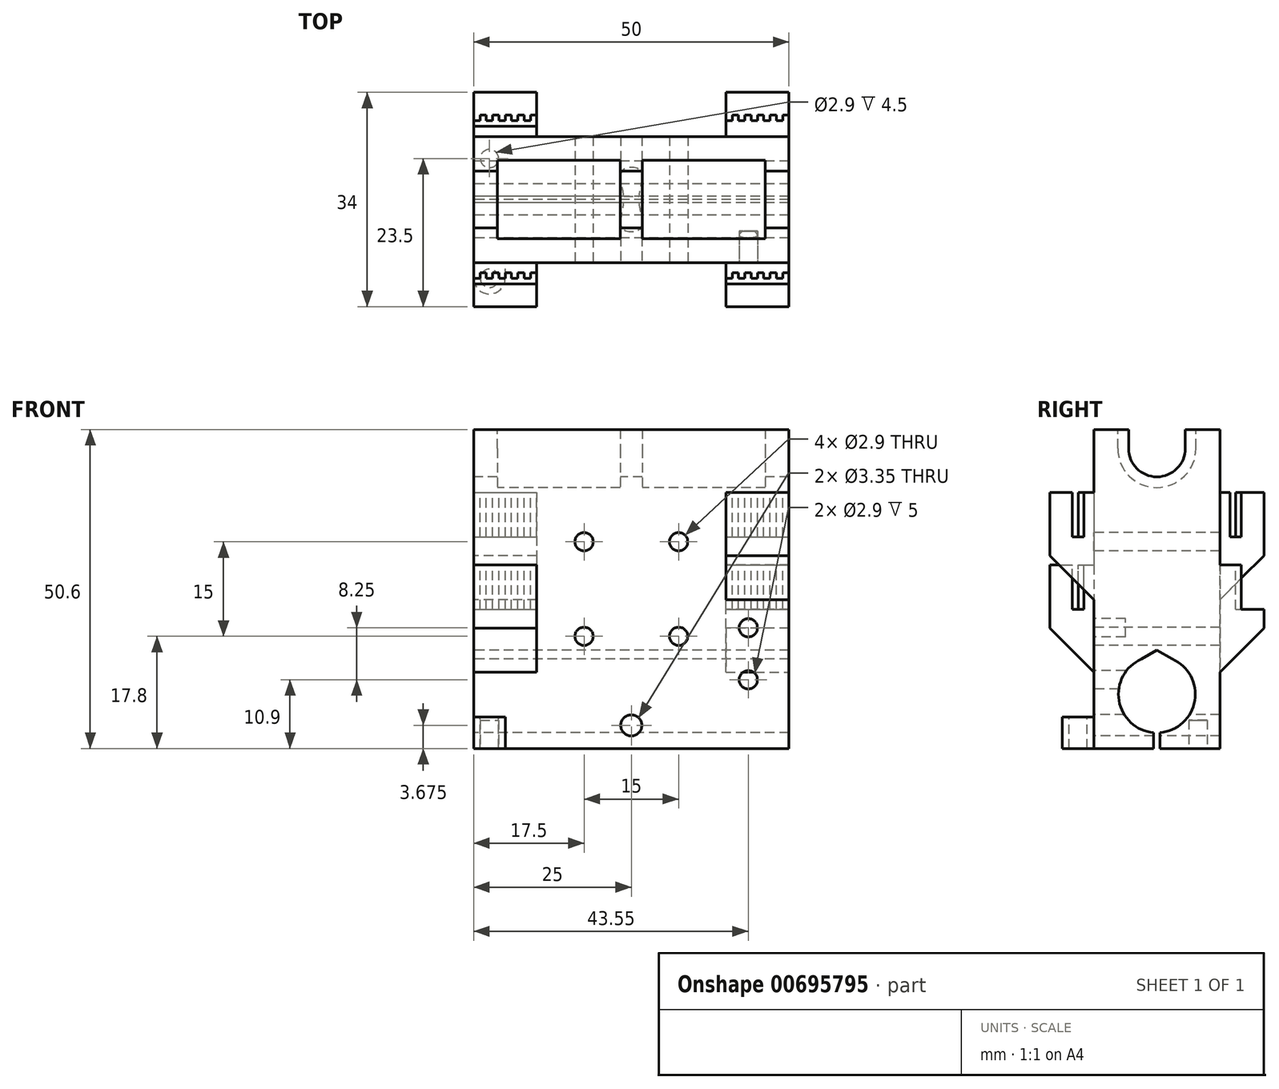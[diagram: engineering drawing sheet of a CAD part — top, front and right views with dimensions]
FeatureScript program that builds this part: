
annotation { "Feature Type Name" : "Feature", "Feature Type Description" : "" }
export const myFeature = defineFeature(function(context is Context, id is Id, definition is map)
    precondition{}
    {
        {
            var Q0;
            Q0=qCreatedBy(makeId("Top.planeOp"),FACE);
            var sketch = newSketch(context, id + "F0", { "sketchPlane" : qUnion([Q0])});
            skLineSegment(sketch, "E0.bottom", {"start": v(0, 0) * mm, "end": v(50, 0) * mm});
            skLineSegment(sketch, "E0.top", {"start": v(0, 20) * mm, "end": v(50, 20) * mm});
            skLineSegment(sketch, "E0.left", {"start": v(0, 0) * mm, "end": v(0, 20) * mm});
            skLineSegment(sketch, "E0.right", {"start": v(50, 0) * mm, "end": v(50, 20) * mm});
            skSolve(sketch);
        }
        {
            var Q0;
            Q0=qSketchRegion(id+"F0",true);
            extrude(context, id + "F1", {"entities" : qUnion([Q0]), "depth" : 50.6 * mm});
        }
        {
            var Q0;
            Q0=makeQuery(id+"F1.opExtrude","SWEPT_FACE",FACE,{"disambiguationData":[OSD([sQuery(id+"F0.wireOp",EDGE,"E0.left")])]});
            var sketch = newSketch(context, id + "F2", { "sketchPlane" : qUnion([Q0])});
            skCircle(sketch, "E1", {"center": v(-10, 8.6) * mm, "radius": 6.1 * mm});
            skCircle(sketch, "E2", {"center": v(-10, 47.6) * mm, "radius": 4.5 * mm});
            skLineSegment(sketch, "E3", {"start": v(-20, 47.6) * mm, "end": v(0, 47.6) * mm, "construction": true});
            skLineSegment(sketch, "E4", {"start": v(-14.5, 50.6) * mm, "end": v(-14.5, 47.6) * mm});
            skLineSegment(sketch, "E5", {"start": v(-5.5, 50.6) * mm, "end": v(-5.5, 47.6) * mm});
            skLineSegment(sketch, "E6", {"start": v(-20, 8.6) * mm, "end": v(0, 8.6) * mm, "construction": true});
            skLineSegment(sketch, "E7", {"start": v(-10, 8.6) * mm, "end": v(-10, 0) * mm, "construction": true});
            skLineSegment(sketch, "E8", {"start": v(-10, 0) * mm, "end": v(-10.5, 0) * mm});
            skLineSegment(sketch, "E9", {"start": v(-10.5, 0) * mm, "end": v(-10.5, 2.52) * mm});
            skLineSegment(sketch, "E10", {"start": v(-10.5, 2.52) * mm, "end": v(-9.5, 2.52) * mm});
            skLineSegment(sketch, "E11", {"start": v(-9.5, 2.52) * mm, "end": v(-9.5, 0) * mm});
            skLineSegment(sketch, "E12", {"start": v(-9.5, 0) * mm, "end": v(-10, 0) * mm});
            skLineSegment(sketch, "E13", {"start": v(-10, 14.7) * mm, "end": v(-10, 15.6) * mm});
            skLineSegment(sketch, "E14", {"start": v(-10, 15.6) * mm, "end": v(-6.39, 13.51) * mm});
            skLineSegment(sketch, "E15", {"start": v(-10, 15.6) * mm, "end": v(-13.61, 13.51) * mm});
            skCircle(sketch, "E16", {"center": v(-10, 47.6) * mm, "radius": 6.2 * mm});
            skLineSegment(sketch, "E17", {"start": v(-3.8, 47.6) * mm, "end": v(-3.8, 50.6) * mm});
            skLineSegment(sketch, "E18", {"start": v(-16.2, 47.6) * mm, "end": v(-16.2, 50.6) * mm});
            skSolve(sketch);
        }
        {
            var Q0;
            {var subQ0=sQuery(id+"F2.wireOp",EDGE,"E14");var subQ1=sQuery(id+"F2.wireOp",EDGE,"E1");var subQ3=makeQuery(id+"F2.imprint","INTERSECT",VERTEX,{"disambiguationData":[OD(0.0)],"derivedFrom":[subQ1,subQ0]});Q0=makeQuery(id+"F2.imprint","IMPRINT",FACE,{"disambiguationData":[TD([[makeQuery(id+"F2.imprint","IMPRINT",EDGE,{"disambiguationData":[TD([[subQ3,-1.0]])],"derivedFrom":subQ1}),1.0]])]});}
            var Q1;
            {var subQ0=sQuery(id+"F2.wireOp",EDGE,"E15");var subQ1=sQuery(id+"F2.wireOp",EDGE,"E1");var subQ3=makeQuery(id+"F2.imprint","INTERSECT",VERTEX,{"disambiguationData":[OD(0.0)],"derivedFrom":[subQ1,subQ0]});Q1=makeQuery(id+"F2.imprint","IMPRINT",FACE,{"disambiguationData":[TD([[makeQuery(id+"F2.imprint","IMPRINT",EDGE,{"disambiguationData":[TD([[subQ3,1.0]])],"derivedFrom":subQ1}),1.0]])]});}
            var Q2;
            Q2=makeQuery(id+"F2.imprint","IMPRINT",FACE,{"disambiguationData":[TD([[makeQuery(id+"F2.imprint","IMPRINT",EDGE,{"derivedFrom":sQuery(id+"F2.wireOp",EDGE,"E8")}),-1.0]])]});
            var Q3;
            {var subQ0=sQuery(id+"F2.wireOp",EDGE,"E10");Q3=makeQuery(id+"F2.imprint","IMPRINT",FACE,{"disambiguationData":[TD([[makeQuery(id+"F2.imprint","IMPRINT",EDGE,{"derivedFrom":subQ0}),-1.0]])]});}
            var Q4;
            {var subQ3=sQuery(id+"F2.wireOp",EDGE,"E13");Q4=makeQuery(id+"F2.imprint","IMPRINT",FACE,{"disambiguationData":[TD([[makeQuery(id+"F2.imprint","IMPRINT",EDGE,{"derivedFrom":subQ3}),-1.0]])]});}
            var Q5;
            {var subQ3=sQuery(id+"F2.wireOp",EDGE,"E13");Q5=makeQuery(id+"F2.imprint","IMPRINT",FACE,{"disambiguationData":[TD([[makeQuery(id+"F2.imprint","IMPRINT",EDGE,{"derivedFrom":subQ3}),1.0]])]});}
            var Q6;
            {var subQ7=sQuery(id+"F2.wireOp",EDGE,"E10");Q6=makeQuery(id+"F2.imprint","IMPRINT",FACE,{"disambiguationData":[TD([[makeQuery(id+"F2.imprint","IMPRINT",EDGE,{"derivedFrom":subQ7}),1.0]])]});}
            var Q7;
            {var subQ3=sQuery(id+"F2.wireOp",EDGE,"E5");Q7=makeQuery(id+"F2.imprint","IMPRINT",FACE,{"disambiguationData":[TD([[makeQuery(id+"F2.imprint","IMPRINT",EDGE,{"derivedFrom":subQ3}),-1.0]])]});}
            var Q8;
            {var subQ0=sQuery(id+"F2.wireOp",EDGE,"E4");Q8=makeQuery(id+"F2.imprint","IMPRINT",FACE,{"disambiguationData":[TD([[makeQuery(id+"F2.imprint","IMPRINT",EDGE,{"derivedFrom":subQ0}),1.0]])]});}
            var Q9;
            {var subQ0=sQuery(id+"F2.wireOp",EDGE,"E4");Q9=makeQuery(id+"F2.imprint","IMPRINT",FACE,{"disambiguationData":[TD([[makeQuery(id+"F2.imprint","IMPRINT",EDGE,{"derivedFrom":subQ0}),1.0]])]});}
            var Q10;
            {var subQ3=sQuery(id+"F2.wireOp",EDGE,"E5");Q10=makeQuery(id+"F2.imprint","IMPRINT",FACE,{"disambiguationData":[TD([[makeQuery(id+"F2.imprint","IMPRINT",EDGE,{"derivedFrom":subQ3}),-1.0]])]});}
            var Q11;
            {var subQ1=sQuery(id+"F2.wireOp",EDGE,"E2");var subQ4=makeQuery(id+"F2.imprint","INTERSECT",VERTEX,{"derivedFrom":[subQ1,sQuery(id+"F2.wireOp",EDGE,"E5")]});Q11=makeQuery(id+"F2.imprint","IMPRINT",FACE,{"disambiguationData":[TD([[makeQuery(id+"F2.imprint","IMPRINT",EDGE,{"disambiguationData":[TD([[subQ4,-1.0]])],"derivedFrom":subQ1}),1.0]])]});}
            extrude(context, id + "F3", {"entities" : qUnion([Q0, Q1, Q2, Q3, Q4, Q5, Q6, Q7, Q8, Q9, Q10, Q11]), "operationType" : NewBodyOperationType.REMOVE, "endBound" : BoundingType.THROUGH_ALL, "oppositeDirection" : true, "depth" : 25 * mm});
        }
        {
            var Q0;
            {var subQ3=sQuery(id+"F2.wireOp",EDGE,"E4");Q0=makeQuery(id+"F2.imprint","IMPRINT",FACE,{"disambiguationData":[TD([[makeQuery(id+"F2.imprint","IMPRINT",EDGE,{"derivedFrom":subQ3}),-1.0]])]});}
            var Q1;
            {var subQ3=sQuery(id+"F2.wireOp",EDGE,"E18");Q1=makeQuery(id+"F2.imprint","IMPRINT",FACE,{"disambiguationData":[TD([[makeQuery(id+"F2.imprint","IMPRINT",EDGE,{"derivedFrom":subQ3}),-1.0]])]});}
            var Q2;
            {var subQ3=sQuery(id+"F2.wireOp",EDGE,"E17");Q2=makeQuery(id+"F2.imprint","IMPRINT",FACE,{"disambiguationData":[TD([[makeQuery(id+"F2.imprint","IMPRINT",EDGE,{"derivedFrom":subQ3}),1.0]])]});}
            extrude(context, id + "F4", {"entities" : qUnion([Q0, Q1, Q2]), "operationType" : NewBodyOperationType.REMOVE, "oppositeDirection" : true, "depth" : 46.25 * mm});
        }
        {
            var Q0;
            {var subQ3=sQuery(id+"F2.wireOp",EDGE,"E4");Q0=makeQuery(id+"F2.imprint","IMPRINT",FACE,{"disambiguationData":[TD([[makeQuery(id+"F2.imprint","IMPRINT",EDGE,{"derivedFrom":subQ3}),-1.0]])]});}
            var Q1;
            {var subQ3=sQuery(id+"F2.wireOp",EDGE,"E18");Q1=makeQuery(id+"F2.imprint","IMPRINT",FACE,{"disambiguationData":[TD([[makeQuery(id+"F2.imprint","IMPRINT",EDGE,{"derivedFrom":subQ3}),-1.0]])]});}
            var Q2;
            {var subQ3=sQuery(id+"F2.wireOp",EDGE,"E17");Q2=makeQuery(id+"F2.imprint","IMPRINT",FACE,{"disambiguationData":[TD([[makeQuery(id+"F2.imprint","IMPRINT",EDGE,{"derivedFrom":subQ3}),1.0]])]});}
            extrude(context, id + "F5", {"entities" : qUnion([Q0, Q1, Q2]), "operationType" : NewBodyOperationType.ADD, "oppositeDirection" : true, "depth" : 26.75 * mm});
        }
        {
            var Q0;
            {var subQ3=sQuery(id+"F2.wireOp",EDGE,"E4");Q0=makeQuery(id+"F2.imprint","IMPRINT",FACE,{"disambiguationData":[TD([[makeQuery(id+"F2.imprint","IMPRINT",EDGE,{"derivedFrom":subQ3}),-1.0]])]});}
            var Q1;
            {var subQ3=sQuery(id+"F2.wireOp",EDGE,"E18");Q1=makeQuery(id+"F2.imprint","IMPRINT",FACE,{"disambiguationData":[TD([[makeQuery(id+"F2.imprint","IMPRINT",EDGE,{"derivedFrom":subQ3}),-1.0]])]});}
            var Q2;
            {var subQ3=sQuery(id+"F2.wireOp",EDGE,"E17");Q2=makeQuery(id+"F2.imprint","IMPRINT",FACE,{"disambiguationData":[TD([[makeQuery(id+"F2.imprint","IMPRINT",EDGE,{"derivedFrom":subQ3}),1.0]])]});}
            extrude(context, id + "F6", {"entities" : qUnion([Q0, Q1, Q2]), "operationType" : NewBodyOperationType.REMOVE, "oppositeDirection" : true, "depth" : 23.25 * mm});
        }
        {
            var Q0;
            {var subQ3=sQuery(id+"F2.wireOp",EDGE,"E4");Q0=makeQuery(id+"F2.imprint","IMPRINT",FACE,{"disambiguationData":[TD([[makeQuery(id+"F2.imprint","IMPRINT",EDGE,{"derivedFrom":subQ3}),-1.0]])]});}
            var Q1;
            {var subQ3=sQuery(id+"F2.wireOp",EDGE,"E18");Q1=makeQuery(id+"F2.imprint","IMPRINT",FACE,{"disambiguationData":[TD([[makeQuery(id+"F2.imprint","IMPRINT",EDGE,{"derivedFrom":subQ3}),-1.0]])]});}
            var Q2;
            {var subQ3=sQuery(id+"F2.wireOp",EDGE,"E17");Q2=makeQuery(id+"F2.imprint","IMPRINT",FACE,{"disambiguationData":[TD([[makeQuery(id+"F2.imprint","IMPRINT",EDGE,{"derivedFrom":subQ3}),1.0]])]});}
            extrude(context, id + "F7", {"entities" : qUnion([Q0, Q1, Q2]), "operationType" : NewBodyOperationType.ADD, "oppositeDirection" : true, "depth" : 3.75 * mm});
        }
        {
            var Q0;
            Q0=makeQuery(id+"F1.opExtrude","SWEPT_FACE",FACE,{"disambiguationData":[OSD([sQuery(id+"F0.wireOp",EDGE,"E0.bottom")])]});
            var sketch = newSketch(context, id + "F8", { "sketchPlane" : qUnion([Q0])});
            skLineSegment(sketch, "E19.bottom", {"start": v(0, 29.1) * mm, "end": v(10, 29.1) * mm});
            skLineSegment(sketch, "E19.top", {"start": v(0, 9.1) * mm, "end": v(10, 9.1) * mm});
            skLineSegment(sketch, "E19.left", {"start": v(0, 29.1) * mm, "end": v(0, 9.1) * mm});
            skLineSegment(sketch, "E19.right", {"start": v(10, 29.1) * mm, "end": v(10, 9.1) * mm});
            skLineSegment(sketch, "E20.bottom", {"start": v(50, 40.6) * mm, "end": v(40, 40.6) * mm});
            skLineSegment(sketch, "E20.top", {"start": v(50, 20.6) * mm, "end": v(40, 20.6) * mm});
            skLineSegment(sketch, "E20.left", {"start": v(50, 40.6) * mm, "end": v(50, 20.6) * mm});
            skLineSegment(sketch, "E20.right", {"start": v(40, 40.6) * mm, "end": v(40, 20.6) * mm});
            skPoint(sketch, "E21", {"position": v(0, 47.6) * mm});
            skPoint(sketch, "E22", {"position": v(0, 8.6) * mm});
            skSolve(sketch);
        }
        {
            var Q0;
            Q0=qSketchRegion(id+"F8",true);
            extrude(context, id + "F9", {"entities" : qUnion([Q0]), "operationType" : NewBodyOperationType.ADD, "depth" : 7 * mm});
        }
        {
            var Q0;
            Q0=makeQuery(id+"F9.opExtrude","CAP_EDGE",EDGE,{"disambiguationData":[OSD([sQuery(id+"F8.wireOp",EDGE,"E19.top")])],"isStart":false});
            var Q1;
            Q1=makeQuery(id+"F9.opExtrude","CAP_EDGE",EDGE,{"disambiguationData":[OSD([sQuery(id+"F8.wireOp",EDGE,"E20.top")])],"isStart":false});
            chamfer(context, id + "F10", {"entities" : qUnion([Q0, Q1]), "width" : 10 * mm, "tangentPropagation" : true});
        }
        {
            var Q0;
            Q0=makeQuery(id+"F9.opExtrude","SWEPT_FACE",FACE,{"disambiguationData":[OSD([sQuery(id+"F8.wireOp",EDGE,"E19.bottom")])]});
            var sketch = newSketch(context, id + "F11", { "sketchPlane" : qUnion([Q0])});
            skLineSegment(sketch, "E23", {"start": v(-935.9, 0) * mm, "end": v(-935.88, -4.54) * mm});
            skLineSegment(sketch, "E24.left", {"start": v(0, -3.4) * mm, "end": v(0, -1.6) * mm});
            skLineSegment(sketch, "E25", {"start": v(6, -2.5) * mm, "end": v(7, -2.5) * mm});
            skLineSegment(sketch, "E26", {"start": v(4, -2.5) * mm, "end": v(5, -2.5) * mm});
            skLineSegment(sketch, "E27", {"start": v(0, -2.5) * mm, "end": v(1, -2.5) * mm});
            skLineSegment(sketch, "E28", {"start": v(7, -1.6) * mm, "end": v(8, -1.6) * mm});
            skLineSegment(sketch, "E29", {"start": v(2, -2.5) * mm, "end": v(3, -2.5) * mm});
            skLineSegment(sketch, "E30", {"start": v(3, -1.6) * mm, "end": v(4, -1.6) * mm});
            skLineSegment(sketch, "E31", {"start": v(8, -2.5) * mm, "end": v(9, -2.5) * mm});
            skLineSegment(sketch, "E32", {"start": v(8, -1.6) * mm, "end": v(8, -2.5) * mm});
            skLineSegment(sketch, "E33", {"start": v(9, -2.5) * mm, "end": v(9, -1.6) * mm});
            skLineSegment(sketch, "E34", {"start": v(10, -1.6) * mm, "end": v(10, -2.5) * mm});
            skLineSegment(sketch, "E35", {"start": v(6, -1.6) * mm, "end": v(6, -2.5) * mm});
            skLineSegment(sketch, "E36", {"start": v(2, -1.6) * mm, "end": v(2, -2.5) * mm});
            skLineSegment(sketch, "E37", {"start": v(1, -1.6) * mm, "end": v(2, -1.6) * mm});
            skLineSegment(sketch, "E38", {"start": v(1, -2.5) * mm, "end": v(1, -1.6) * mm});
            skLineSegment(sketch, "E39", {"start": v(9, -1.6) * mm, "end": v(10, -1.6) * mm});
            skLineSegment(sketch, "E40", {"start": v(5, -1.6) * mm, "end": v(6, -1.6) * mm});
            skLineSegment(sketch, "E41", {"start": v(5, -2.5) * mm, "end": v(5, -1.6) * mm});
            skLineSegment(sketch, "E42", {"start": v(3, -2.5) * mm, "end": v(3, -1.6) * mm});
            skLineSegment(sketch, "E43", {"start": v(4, -1.6) * mm, "end": v(4, -2.5) * mm});
            skLineSegment(sketch, "E44", {"start": v(7, -2.5) * mm, "end": v(7, -1.6) * mm});
            skLineSegment(sketch, "E45", {"start": v(0, -1.6) * mm, "end": v(0, -2.5) * mm});
            skLineSegment(sketch, "E46", {"start": v(10, -2.5) * mm, "end": v(10, -3.4) * mm});
            skLineSegment(sketch, "E47", {"start": v(0, -3.4) * mm, "end": v(10, -3.4) * mm});
            skLineSegment(sketch, "E48", {"start": v(5.3, -1.6) * mm, "end": v(5.3, 0) * mm});
            skSolve(sketch);
        }
        {
            var Q0;
            Q0=qSketchRegion(id+"F11",true);
            extrude(context, id + "F12", {"entities" : qUnion([Q0]), "operationType" : NewBodyOperationType.REMOVE, "oppositeDirection" : true, "depth" : 7 * mm});
        }
        {
            var Q0;
            Q0=makeQuery(id+"F9.opExtrude","SWEPT_FACE",FACE,{"disambiguationData":[OSD([sQuery(id+"F8.wireOp",EDGE,"E20.bottom")])]});
            var sketch = newSketch(context, id + "F13", { "sketchPlane" : qUnion([Q0])});
            skLineSegment(sketch, "E49.left", {"start": v(40, -3.4) * mm, "end": v(40, -1.6) * mm});
            skLineSegment(sketch, "E50", {"start": v(46, -2.5) * mm, "end": v(47, -2.5) * mm});
            skLineSegment(sketch, "E51", {"start": v(44, -2.5) * mm, "end": v(45, -2.5) * mm});
            skLineSegment(sketch, "E52", {"start": v(40, -2.5) * mm, "end": v(41, -2.5) * mm});
            skLineSegment(sketch, "E53", {"start": v(47, -1.6) * mm, "end": v(48, -1.6) * mm});
            skLineSegment(sketch, "E54", {"start": v(42, -2.5) * mm, "end": v(43, -2.5) * mm});
            skLineSegment(sketch, "E55", {"start": v(43, -1.6) * mm, "end": v(44, -1.6) * mm});
            skLineSegment(sketch, "E56", {"start": v(48, -2.5) * mm, "end": v(49, -2.5) * mm});
            skLineSegment(sketch, "E57", {"start": v(48, -1.6) * mm, "end": v(48, -2.5) * mm});
            skLineSegment(sketch, "E58", {"start": v(49, -2.5) * mm, "end": v(49, -1.6) * mm});
            skLineSegment(sketch, "E59", {"start": v(50, -1.6) * mm, "end": v(50, -2.5) * mm});
            skLineSegment(sketch, "E60", {"start": v(46, -1.6) * mm, "end": v(46, -2.5) * mm});
            skLineSegment(sketch, "E61", {"start": v(42, -1.6) * mm, "end": v(42, -2.5) * mm});
            skLineSegment(sketch, "E62", {"start": v(41, -1.6) * mm, "end": v(42, -1.6) * mm});
            skLineSegment(sketch, "E63", {"start": v(41, -2.5) * mm, "end": v(41, -1.6) * mm});
            skLineSegment(sketch, "E64", {"start": v(49, -1.6) * mm, "end": v(50, -1.6) * mm});
            skLineSegment(sketch, "E65", {"start": v(45, -1.6) * mm, "end": v(46, -1.6) * mm});
            skLineSegment(sketch, "E66", {"start": v(45, -2.5) * mm, "end": v(45, -1.6) * mm});
            skLineSegment(sketch, "E67", {"start": v(43, -2.5) * mm, "end": v(43, -1.6) * mm});
            skLineSegment(sketch, "E68", {"start": v(44, -1.6) * mm, "end": v(44, -2.5) * mm});
            skLineSegment(sketch, "E69", {"start": v(47, -2.5) * mm, "end": v(47, -1.6) * mm});
            skLineSegment(sketch, "E70", {"start": v(40, -1.6) * mm, "end": v(40, -2.5) * mm});
            skLineSegment(sketch, "E71", {"start": v(50, -2.5) * mm, "end": v(50, -3.4) * mm});
            skLineSegment(sketch, "E72", {"start": v(40, -3.4) * mm, "end": v(50, -3.4) * mm});
            skLineSegment(sketch, "E73", {"start": v(45.23, -1.6) * mm, "end": v(45.23, 0) * mm});
            skSolve(sketch);
        }
        {
            var Q0;
            Q0=qSketchRegion(id+"F13",true);
            extrude(context, id + "F14", {"entities" : qUnion([Q0]), "operationType" : NewBodyOperationType.REMOVE, "oppositeDirection" : true, "depth" : 7 * mm});
        }
        {
            var Q0;
            Q0=makeQuery(id+"F1.opExtrude","SWEPT_FACE",FACE,{"disambiguationData":[OSD([sQuery(id+"F0.wireOp",EDGE,"E0.top")])]});
            var sketch = newSketch(context, id + "F15", { "sketchPlane" : qUnion([Q0])});
            skLineSegment(sketch, "E74.bottom", {"start": v(-50, 9.1) * mm, "end": v(-40, 9.1) * mm});
            skLineSegment(sketch, "E74.top", {"start": v(-50, 29.1) * mm, "end": v(-40, 29.1) * mm});
            skLineSegment(sketch, "E74.left", {"start": v(-50, 9.1) * mm, "end": v(-50, 29.1) * mm});
            skLineSegment(sketch, "E74.right", {"start": v(-40, 9.1) * mm, "end": v(-40, 29.1) * mm});
            skLineSegment(sketch, "E75.bottom", {"start": v(0, 40.6) * mm, "end": v(-10, 40.6) * mm});
            skLineSegment(sketch, "E75.top", {"start": v(0, 20.6) * mm, "end": v(-10, 20.6) * mm});
            skLineSegment(sketch, "E75.left", {"start": v(0, 40.6) * mm, "end": v(0, 20.6) * mm});
            skLineSegment(sketch, "E75.right", {"start": v(-10, 40.6) * mm, "end": v(-10, 20.6) * mm});
            skSolve(sketch);
        }
        {
            var Q0;
            Q0=qSketchRegion(id+"F15",true);
            extrude(context, id + "F16", {"entities" : qUnion([Q0]), "operationType" : NewBodyOperationType.ADD, "depth" : 7 * mm});
        }
        {
            var Q0;
            Q0=makeQuery(id+"F16.opExtrude","SWEPT_FACE",FACE,{"disambiguationData":[OSD([sQuery(id+"F15.wireOp",EDGE,"E74.top")])]});
            var sketch = newSketch(context, id + "F17", { "sketchPlane" : qUnion([Q0])});
            skLineSegment(sketch, "E76.left", {"start": v(40, 21.6) * mm, "end": v(40, 23.4) * mm});
            skLineSegment(sketch, "E77", {"start": v(46, 22.5) * mm, "end": v(47, 22.5) * mm});
            skLineSegment(sketch, "E78", {"start": v(44, 22.5) * mm, "end": v(45, 22.5) * mm});
            skLineSegment(sketch, "E79", {"start": v(40, 22.5) * mm, "end": v(41, 22.5) * mm});
            skLineSegment(sketch, "E80", {"start": v(47, 23.4) * mm, "end": v(48, 23.4) * mm});
            skLineSegment(sketch, "E81", {"start": v(42, 22.5) * mm, "end": v(43, 22.5) * mm});
            skLineSegment(sketch, "E82", {"start": v(43, 23.4) * mm, "end": v(44, 23.4) * mm});
            skLineSegment(sketch, "E83", {"start": v(48, 22.5) * mm, "end": v(49, 22.5) * mm});
            skLineSegment(sketch, "E84", {"start": v(48, 23.4) * mm, "end": v(48, 22.5) * mm});
            skLineSegment(sketch, "E85", {"start": v(49, 22.5) * mm, "end": v(49, 23.4) * mm});
            skLineSegment(sketch, "E86", {"start": v(50, 23.4) * mm, "end": v(50, 22.5) * mm});
            skLineSegment(sketch, "E87", {"start": v(46, 23.4) * mm, "end": v(46, 22.5) * mm});
            skLineSegment(sketch, "E88", {"start": v(42, 23.4) * mm, "end": v(42, 22.5) * mm});
            skLineSegment(sketch, "E89", {"start": v(41, 23.4) * mm, "end": v(42, 23.4) * mm});
            skLineSegment(sketch, "E90", {"start": v(41, 22.5) * mm, "end": v(41, 23.4) * mm});
            skLineSegment(sketch, "E91", {"start": v(49, 23.4) * mm, "end": v(50, 23.4) * mm});
            skLineSegment(sketch, "E92", {"start": v(45, 23.4) * mm, "end": v(46, 23.4) * mm});
            skLineSegment(sketch, "E93", {"start": v(45, 22.5) * mm, "end": v(45, 23.4) * mm});
            skLineSegment(sketch, "E94", {"start": v(43, 22.5) * mm, "end": v(43, 23.4) * mm});
            skLineSegment(sketch, "E95", {"start": v(44, 23.4) * mm, "end": v(44, 22.5) * mm});
            skLineSegment(sketch, "E96", {"start": v(47, 22.5) * mm, "end": v(47, 23.4) * mm});
            skLineSegment(sketch, "E97", {"start": v(40, 23.4) * mm, "end": v(40, 22.5) * mm});
            skLineSegment(sketch, "E98", {"start": v(50, 22.5) * mm, "end": v(50, 21.6) * mm});
            skLineSegment(sketch, "E99", {"start": v(40, 21.6) * mm, "end": v(50, 21.6) * mm});
            skLineSegment(sketch, "E100", {"start": v(45, 21.6) * mm, "end": v(45, 20) * mm});
            skSolve(sketch);
        }
        {
            var Q0;
            {var subQ4=sQuery(id+"F17.wireOp",EDGE,"E76.left");Q0=makeQuery(id+"F17.imprint","IMPRINT",FACE,{"disambiguationData":[TD([[makeQuery(id+"F17.imprint","IMPRINT",EDGE,{"derivedFrom":subQ4}),1.0]])]});}
            extrude(context, id + "F18", {"entities" : qUnion([Q0]), "operationType" : NewBodyOperationType.REMOVE, "oppositeDirection" : true, "depth" : 7 * mm});
        }
        {
            var Q0;
            Q0=makeQuery(id+"F16.opExtrude","SWEPT_FACE",FACE,{"disambiguationData":[OSD([sQuery(id+"F15.wireOp",EDGE,"E75.bottom")])]});
            var sketch = newSketch(context, id + "F19", { "sketchPlane" : qUnion([Q0])});
            skLineSegment(sketch, "E101", {"start": v(6, 22.5) * mm, "end": v(7, 22.5) * mm});
            skLineSegment(sketch, "E102", {"start": v(4, 22.5) * mm, "end": v(5, 22.5) * mm});
            skLineSegment(sketch, "E103", {"start": v(0, 22.5) * mm, "end": v(1, 22.5) * mm});
            skLineSegment(sketch, "E104", {"start": v(7, 23.4) * mm, "end": v(8, 23.4) * mm});
            skLineSegment(sketch, "E105", {"start": v(2, 22.5) * mm, "end": v(3, 22.5) * mm});
            skLineSegment(sketch, "E106", {"start": v(3, 23.4) * mm, "end": v(4, 23.4) * mm});
            skLineSegment(sketch, "E107", {"start": v(8, 22.5) * mm, "end": v(9, 22.5) * mm});
            skLineSegment(sketch, "E108", {"start": v(8, 23.4) * mm, "end": v(8, 22.5) * mm});
            skLineSegment(sketch, "E109", {"start": v(9, 22.5) * mm, "end": v(9, 23.4) * mm});
            skLineSegment(sketch, "E110", {"start": v(10, 23.4) * mm, "end": v(10, 22.5) * mm});
            skLineSegment(sketch, "E111", {"start": v(6, 23.4) * mm, "end": v(6, 22.5) * mm});
            skLineSegment(sketch, "E112", {"start": v(2, 23.4) * mm, "end": v(2, 22.5) * mm});
            skLineSegment(sketch, "E113", {"start": v(1, 23.4) * mm, "end": v(2, 23.4) * mm});
            skLineSegment(sketch, "E114", {"start": v(1, 22.5) * mm, "end": v(1, 23.4) * mm});
            skLineSegment(sketch, "E115", {"start": v(9, 23.4) * mm, "end": v(10, 23.4) * mm});
            skLineSegment(sketch, "E116", {"start": v(5, 23.4) * mm, "end": v(6, 23.4) * mm});
            skLineSegment(sketch, "E117", {"start": v(5, 22.5) * mm, "end": v(5, 23.4) * mm});
            skLineSegment(sketch, "E118", {"start": v(3, 22.5) * mm, "end": v(3, 23.4) * mm});
            skLineSegment(sketch, "E119", {"start": v(4, 23.4) * mm, "end": v(4, 22.5) * mm});
            skLineSegment(sketch, "E120", {"start": v(7, 22.5) * mm, "end": v(7, 23.4) * mm});
            skLineSegment(sketch, "E121", {"start": v(10, 22.5) * mm, "end": v(10, 21.6) * mm});
            skLineSegment(sketch, "E122", {"start": v(0, 21.6) * mm, "end": v(10, 21.6) * mm});
            skLineSegment(sketch, "E123", {"start": v(5, 21.6) * mm, "end": v(5, 20) * mm});
            skLineSegment(sketch, "E124", {"start": v(0, 21.6) * mm, "end": v(0, 22.5) * mm});
            skSolve(sketch);
        }
        {
            var Q0;
            Q0=makeQuery(id+"F19.imprint","IMPRINT",FACE,{"disambiguationData":[TD([[makeQuery(id+"F19.imprint","IMPRINT",EDGE,{"derivedFrom":sQuery(id+"F19.wireOp",EDGE,"E101")}),-1.0]])]});
            extrude(context, id + "F20", {"entities" : qUnion([Q0]), "operationType" : NewBodyOperationType.REMOVE, "oppositeDirection" : true, "depth" : 7 * mm});
        }
        {
            var Q0;
            Q0=makeQuery(id+"F16.opExtrude","CAP_EDGE",EDGE,{"disambiguationData":[OSD([sQuery(id+"F15.wireOp",EDGE,"E75.top")])],"isStart":false});
            var Q1;
            Q1=makeQuery(id+"F16.opExtrude","CAP_EDGE",EDGE,{"disambiguationData":[OSD([sQuery(id+"F15.wireOp",EDGE,"E74.bottom")])],"isStart":false});
            chamfer(context, id + "F21", {"entities" : qUnion([Q0, Q1]), "width" : 10 * mm, "tangentPropagation" : true});
        }
        {
            var Q0;
            Q0=makeQuery(id+"F1.opExtrude","SWEPT_FACE",FACE,{"disambiguationData":[OSD([sQuery(id+"F0.wireOp",EDGE,"E0.bottom")])]});
            var sketch = newSketch(context, id + "F22", { "sketchPlane" : qUnion([Q0])});
            skCircle(sketch, "E125", {"center": v(17.5, 32.8) * mm, "radius": 1.45 * mm});
            skCircle(sketch, "E126", {"center": v(32.5, 32.8) * mm, "radius": 1.45 * mm});
            skCircle(sketch, "E127", {"center": v(17.5, 17.8) * mm, "radius": 1.45 * mm});
            skCircle(sketch, "E128", {"center": v(32.5, 17.8) * mm, "radius": 1.45 * mm});
            skLineSegment(sketch, "E129", {"start": v(17.5, 32.8) * mm, "end": v(0, 32.8) * mm});
            skLineSegment(sketch, "E130", {"start": v(32.5, 17.8) * mm, "end": v(50, 17.8) * mm});
            skLineSegment(sketch, "E131", {"start": v(32.5, 32.8) * mm, "end": v(32.5, 50.6) * mm});
            skLineSegment(sketch, "E132", {"start": v(17.5, 17.8) * mm, "end": v(17.5, 0) * mm});
            skCircle(sketch, "E133", {"center": v(25, 3.68) * mm, "radius": 1.68 * mm});
            skLineSegment(sketch, "E134", {"start": v(25, 0) * mm, "end": v(25, 13.82) * mm, "construction": true});
            skSolve(sketch);
        }
        {
            var Q0;
            Q0=qSketchRegion(id+"F22",true);
            var Q1;
            Q1=makeQuery(id+"F22.imprint","IMPRINT",FACE,{"disambiguationData":[TD([[makeQuery(id+"F22.imprint","IMPRINT",EDGE,{"derivedFrom":sQuery(id+"F22.wireOp",EDGE,"E125")}),1.0]])]});
            var Q2;
            Q2=makeQuery(id+"F22.imprint","IMPRINT",FACE,{"disambiguationData":[TD([[makeQuery(id+"F22.imprint","IMPRINT",EDGE,{"derivedFrom":sQuery(id+"F22.wireOp",EDGE,"E126")}),1.0]])]});
            var Q3;
            Q3=makeQuery(id+"F22.imprint","IMPRINT",FACE,{"disambiguationData":[TD([[makeQuery(id+"F22.imprint","IMPRINT",EDGE,{"derivedFrom":sQuery(id+"F22.wireOp",EDGE,"E128")}),1.0]])]});
            var Q4;
            Q4=makeQuery(id+"F22.imprint","IMPRINT",FACE,{"disambiguationData":[TD([[makeQuery(id+"F22.imprint","IMPRINT",EDGE,{"derivedFrom":sQuery(id+"F22.wireOp",EDGE,"E127")}),1.0]])]});
            extrude(context, id + "F23", {"entities" : qUnion([Q0, Q1, Q2, Q3, Q4]), "operationType" : NewBodyOperationType.REMOVE, "endBound" : BoundingType.THROUGH_ALL, "oppositeDirection" : true, "depth" : 25 * mm});
        }
        {
            var Q0;
            Q0=makeQuery(id+"F1.opExtrude","SWEPT_FACE",FACE,{"disambiguationData":[OSD([sQuery(id+"F0.wireOp",EDGE,"E0.bottom")])]});
            var sketch = newSketch(context, id + "F24", { "sketchPlane" : qUnion([Q0])});
            skCircle(sketch, "E135", {"center": v(43.55, 19.15) * mm, "radius": 1.45 * mm});
            skCircle(sketch, "E136", {"center": v(43.55, 10.9) * mm, "radius": 1.45 * mm});
            skSolve(sketch);
        }
        {
            var Q0;
            Q0=qSketchRegion(id+"F24",true);
            extrude(context, id + "F25", {"entities" : qUnion([Q0]), "operationType" : NewBodyOperationType.REMOVE, "oppositeDirection" : true, "depth" : 5 * mm});
        }
        {
            var Q0;
            Q0=makeQuery(id+"F1.opExtrude","SWEPT_FACE",FACE,{"disambiguationData":[OSD([sQuery(id+"F0.wireOp",EDGE,"E0.bottom")])]});
            var sketch = newSketch(context, id + "F26", { "sketchPlane" : qUnion([Q0])});
            skLineSegment(sketch, "E137.bottom", {"start": v(0, 0) * mm, "end": v(5, 0) * mm});
            skLineSegment(sketch, "E137.top", {"start": v(0, 5) * mm, "end": v(5, 5) * mm});
            skLineSegment(sketch, "E137.left", {"start": v(0, 0) * mm, "end": v(0, 5) * mm});
            skLineSegment(sketch, "E137.right", {"start": v(5, 0) * mm, "end": v(5, 5) * mm});
            skSolve(sketch);
        }
        {
            var Q0;
            Q0=qSketchRegion(id+"F26",true);
            extrude(context, id + "F27", {"entities" : qUnion([Q0]), "operationType" : NewBodyOperationType.ADD, "depth" : 5 * mm});
        }
        {
            var Q0;
            Q0=makeQuery(id+"F27.opExtrude","SWEPT_FACE",FACE,{"disambiguationData":[OSD([sQuery(id+"F26.wireOp",EDGE,"E137.top")])]});
            var sketch = newSketch(context, id + "F28", { "sketchPlane" : qUnion([Q0])});
            skCircle(sketch, "E138", {"center": v(2.5, -2.5) * mm, "radius": 1.45 * mm});
            skLineSegment(sketch, "E139", {"start": v(0, -2.5) * mm, "end": v(5, -2.5) * mm});
            skSolve(sketch);
        }
        {
            var Q0;
            Q0=qSketchRegion(id+"F28",true);
            extrude(context, id + "F29", {"entities" : qUnion([Q0]), "operationType" : NewBodyOperationType.REMOVE, "oppositeDirection" : true, "depth" : 25 * mm});
        }
        {
            var Q0;
            Q0=makeQuery(id+"F27.opExtrude","CAP_EDGE",EDGE,{"disambiguationData":[OSD([sQuery(id+"F26.wireOp",EDGE,"E137.left")])],"isStart":false});
            var Q1;
            Q1=makeQuery(id+"F27.opExtrude","CAP_EDGE",EDGE,{"disambiguationData":[OSD([sQuery(id+"F26.wireOp",EDGE,"E137.right")])],"isStart":false});
            fillet(context, id + "F30", {"entities" : qUnion([Q0, Q1]), "radius" : 2.5 * mm, "tangentPropagation" : true, "allowEdgeOverflow" : false});
        }
        {
            var Q0;
            {var subQ0=sQuery(id+"F0.wireOp",EDGE,"E0.bottom");var subQ1=sQuery(id+"F0.wireOp",EDGE,"E0.right");var subQ2=sQuery(id+"F0.wireOp",EDGE,"E0.left");Q0=makeQuery(id+"F27.boolean.opBoolean","MERGE",FACE,{"derivedFrom":[makeQuery(id+"F3.boolean.opBoolean","SPLIT",FACE,{"disambiguationData":[TD([makeQuery(id+"F1.opExtrude","SWEPT_FACE",FACE,{"disambiguationData":[OSD([subQ0])]})])],"derivedFrom":makeQuery(id+"F1.opExtrude","CAP_FACE",FACE,{"disambiguationData":[OSD([subQ0,sQuery(id+"F0.wireOp",EDGE,"E0.top"),subQ2,subQ1])],"isStart":true})}),makeQuery(id+"F27.opExtrude","SWEPT_FACE",FACE,{"disambiguationData":[OSD([sQuery(id+"F26.wireOp",EDGE,"E137.bottom")])]})]});}
            var sketch = newSketch(context, id + "F31", { "sketchPlane" : qUnion([Q0])});
            skLineSegment(sketch, "E140", {"start": v(2.5, 2.5) * mm, "end": v(2.5, -16.5) * mm});
            skCircle(sketch, "E141", {"center": v(2.5, -16.5) * mm, "radius": 1.45 * mm});
            skSolve(sketch);
        }
        {
            var Q0;
            Q0=makeQuery(id+"F31.imprint","IMPRINT",FACE,{"disambiguationData":[TD([[makeQuery(id+"F31.imprint","IMPRINT",EDGE,{"derivedFrom":sQuery(id+"F31.wireOp",EDGE,"E141")}),1.0]])]});
            extrude(context, id + "F32", {"entities" : qUnion([Q0]), "operationType" : NewBodyOperationType.REMOVE, "oppositeDirection" : true, "depth" : 4.5 * mm, "offsetDistance" : 25 * mm});
        }
    });
